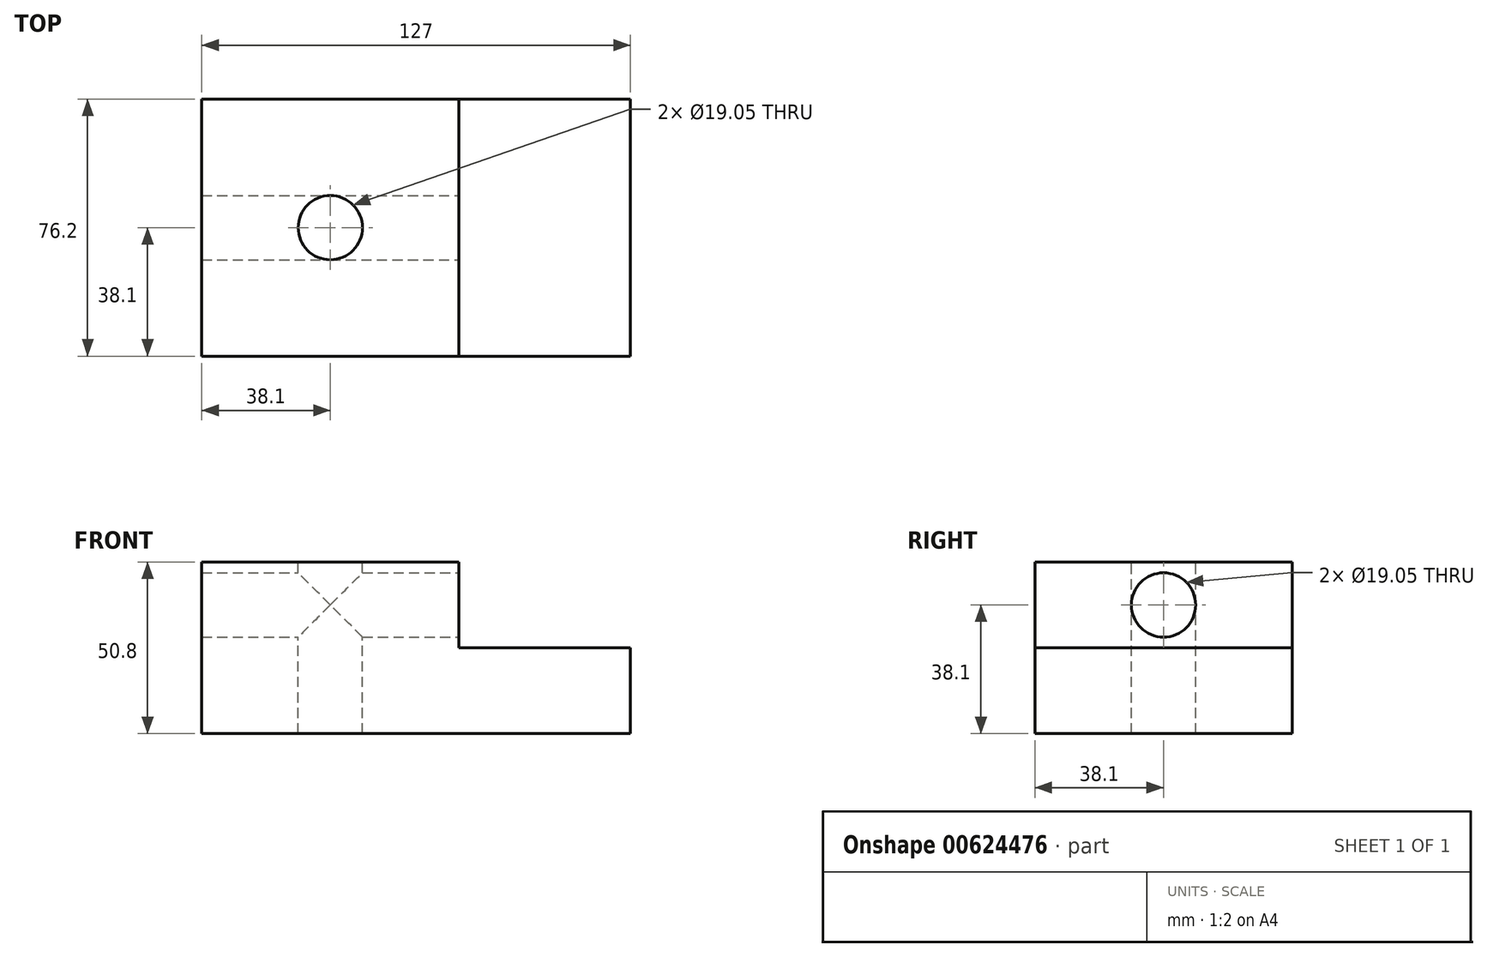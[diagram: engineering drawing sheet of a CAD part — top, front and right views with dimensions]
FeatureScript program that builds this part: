
annotation { "Feature Type Name" : "Feature", "Feature Type Description" : "" }
export const myFeature = defineFeature(function(context is Context, id is Id, definition is map)
    precondition{}
    {
        {
            var Q0;
            Q0=qCreatedBy(makeId("Front.planeOp"),FACE);
            var sketch = newSketch(context, id + "F0", { "sketchPlane" : qUnion([Q0])});
            skLineSegment(sketch, "E0.bottom", {"start": v(0, 0) * mm, "end": v(127, 0) * mm});
            skLineSegment(sketch, "E0.top", {"start": v(0, 50.8) * mm, "end": v(127, 50.8) * mm});
            skLineSegment(sketch, "E0.left", {"start": v(0, 0) * mm, "end": v(0, 50.8) * mm});
            skLineSegment(sketch, "E0.right", {"start": v(127, 0) * mm, "end": v(127, 50.8) * mm});
            skLineSegment(sketch, "E1.bottom", {"start": v(127, 25.4) * mm, "end": v(76.2, 25.4) * mm});
            skLineSegment(sketch, "E1.top", {"start": v(127, 50.8) * mm, "end": v(76.2, 50.8) * mm});
            skLineSegment(sketch, "E1.left", {"start": v(127, 25.4) * mm, "end": v(127, 50.8) * mm});
            skLineSegment(sketch, "E1.right", {"start": v(76.2, 25.4) * mm, "end": v(76.2, 50.8) * mm});
            skSolve(sketch);
        }
        {
            var Q0;
            Q0=makeQuery(id+"F0.imprint","IMPRINT",FACE,{"disambiguationData":[TD([[makeQuery(id+"F0.imprint","IMPRINT",EDGE,{"derivedFrom":sQuery(id+"F0.wireOp",EDGE,"E0.bottom")}),1.0]])]});
            extrude(context, id + "F1", {"entities" : qUnion([Q0]), "depth" : 76.2 * mm, "offsetDistance" : 25.4 * mm});
        }
        {
            var Q0;
            Q0=makeQuery(id+"F1.opExtrude","SWEPT_FACE",FACE,{"disambiguationData":[OSD([sQuery(id+"F0.wireOp",EDGE,"E0.top")])]});
            var sketch = newSketch(context, id + "F2", { "sketchPlane" : qUnion([Q0])});
            skPoint(sketch, "E2", {"position": v(0, -38.1) * mm});
            skPoint(sketch, "E3", {"position": v(38.1, 0) * mm});
            skPoint(sketch, "E4", {"position": v(38.1, -38.1) * mm});
            skSolve(sketch);
        }
        {
            var Q0;
            Q0=makeQuery(id+"F1.opExtrude","SWEPT_FACE",FACE,{"disambiguationData":[OSD([sQuery(id+"F0.wireOp",EDGE,"E1.right")])]});
            var sketch = newSketch(context, id + "F3", { "sketchPlane" : qUnion([Q0])});
            skPoint(sketch, "E5", {"position": v(-38.1, 38.1) * mm});
            skPoint(sketch, "E5.positionSnap0", {"position": v(-38.1, 50.8) * mm});
            skPoint(sketch, "E5.positionSnap1", {"position": v(-76.2, 38.1) * mm});
            skSolve(sketch);
        }
        {
            var Q0;
            Q0=sQuery(id+"F3.wireOp",VERTEX,"E5");
            var Q1;
            Q1=makeQuery(id+"F1.opExtrude","SWEPT_BODY",BODY,{"disambiguationData":[OSD([sQuery(id+"F0.wireOp",EDGE,"E0.bottom"),sQuery(id+"F0.wireOp",EDGE,"E0.top"),sQuery(id+"F0.wireOp",EDGE,"E0.left"),sQuery(id+"F0.wireOp",EDGE,"E0.right"),sQuery(id+"F0.wireOp",EDGE,"E1.bottom"),sQuery(id+"F0.wireOp",EDGE,"E1.right")])]});
            hole(context, id + "F4", {"style" : HoleStyle.SIMPLE, "endStyle" : HoleEndStyle.THROUGH, "holeDiameter" : 19.05 * mm, "majorDiameter" : 6.35 * mm, "isTappedThrough" : true, "tappedDepth" : 12.7 * mm, "tapClearance" : 3, "locations" : qUnion([Q0]), "scope" : qUnion([Q1])});
        }
        {
            var Q0;
            Q0=sQuery(id+"F2.wireOp",VERTEX,"E4");
            var Q1;
            Q1=makeQuery(id+"F1.opExtrude","SWEPT_BODY",BODY,{"disambiguationData":[OSD([sQuery(id+"F0.wireOp",EDGE,"E0.bottom"),sQuery(id+"F0.wireOp",EDGE,"E0.top"),sQuery(id+"F0.wireOp",EDGE,"E0.left"),sQuery(id+"F0.wireOp",EDGE,"E0.right"),sQuery(id+"F0.wireOp",EDGE,"E1.bottom"),sQuery(id+"F0.wireOp",EDGE,"E1.right")])]});
            hole(context, id + "F5", {"style" : HoleStyle.SIMPLE, "endStyle" : HoleEndStyle.THROUGH, "holeDiameter" : 19.05 * mm, "majorDiameter" : 6.35 * mm, "isTappedThrough" : true, "tappedDepth" : 12.7 * mm, "tapClearance" : 3, "locations" : qUnion([Q0]), "scope" : qUnion([Q1])});
        }
    });
